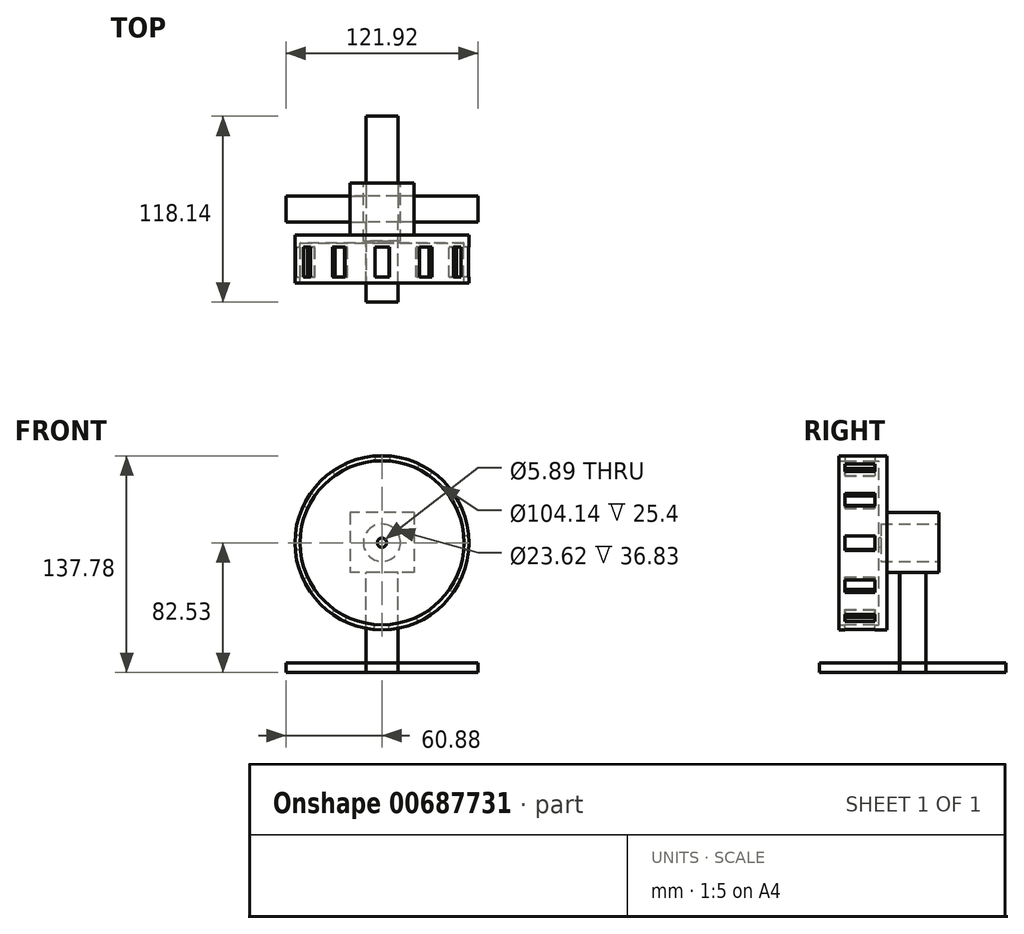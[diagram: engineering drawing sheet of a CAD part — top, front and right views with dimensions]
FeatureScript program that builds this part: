
annotation { "Feature Type Name" : "Feature", "Feature Type Description" : "" }
export const myFeature = defineFeature(function(context is Context, id is Id, definition is map)
    precondition{}
    {
        {
            var Q0;
            Q0=qCreatedBy(makeId("Front.planeOp"),FACE);
            var sketch = newSketch(context, id + "F0", { "sketchPlane" : qUnion([Q0])});
            skCircle(sketch, "E0", {"center": v(0, 0) * mm, "radius": 52.07 * mm});
            skCircle(sketch, "E1", {"center": v(0, 0) * mm, "radius": 55.24 * mm});
            skSolve(sketch);
        }
        {
            var Q0;
            Q0=makeQuery(id+"F0.imprint","IMPRINT",FACE,{"disambiguationData":[TD([[makeQuery(id+"F0.imprint","IMPRINT",EDGE,{"derivedFrom":sQuery(id+"F0.wireOp",EDGE,"E0")}),1.0]])]});
            extrude(context, id + "F1", {"entities" : qUnion([Q0]), "depth" : 5.08 * mm, "offsetDistance" : 25.4 * mm});
        }
        {
            var Q0;
            Q0=makeQuery(id+"F0.imprint","IMPRINT",FACE,{"disambiguationData":[TD([[makeQuery(id+"F0.imprint","IMPRINT",EDGE,{"derivedFrom":sQuery(id+"F0.wireOp",EDGE,"E0")}),-1.0]])]});
            extrude(context, id + "F2", {"entities" : qUnion([Q0]), "operationType" : NewBodyOperationType.ADD, "depth" : 30.48 * mm, "offsetDistance" : 25.4 * mm});
        }
        {
            var Q0;
            Q0=makeQuery(id+"F1.opExtrude","CAP_FACE",FACE,{"disambiguationData":[OSD([sQuery(id+"F0.wireOp",EDGE,"E0")])],"isStart":false});
            var sketch = newSketch(context, id + "F3", { "sketchPlane" : qUnion([Q0])});
            skCircle(sketch, "E2.cCircle", {"center": v(0, 0) * mm, "radius": 17.26 * mm, "construction": true});
            skLineSegment(sketch, "E2.0", {"start": v(12.58, -12.7) * mm, "end": v(4.55, -17.28) * mm});
            skLineSegment(sketch, "E2.1", {"start": v(4.55, -17.28) * mm, "end": v(-4.7, -17.24) * mm});
            skLineSegment(sketch, "E2.2", {"start": v(-4.7, -17.24) * mm, "end": v(-12.7, -12.58) * mm});
            skLineSegment(sketch, "E2.3", {"start": v(-12.7, -12.58) * mm, "end": v(-17.28, -4.55) * mm});
            skLineSegment(sketch, "E2.4", {"start": v(-17.28, -4.55) * mm, "end": v(-17.24, 4.7) * mm});
            skLineSegment(sketch, "E2.5", {"start": v(-17.24, 4.7) * mm, "end": v(-12.58, 12.7) * mm});
            skLineSegment(sketch, "E2.6", {"start": v(-12.58, 12.7) * mm, "end": v(-4.55, 17.28) * mm});
            skLineSegment(sketch, "E2.7", {"start": v(-4.55, 17.28) * mm, "end": v(4.7, 17.24) * mm});
            skLineSegment(sketch, "E2.8", {"start": v(4.7, 17.24) * mm, "end": v(12.7, 12.58) * mm});
            skLineSegment(sketch, "E2.9", {"start": v(12.7, 12.58) * mm, "end": v(17.28, 4.55) * mm});
            skLineSegment(sketch, "E2.10", {"start": v(17.28, 4.55) * mm, "end": v(17.24, -4.7) * mm});
            skLineSegment(sketch, "E2.11", {"start": v(17.24, -4.7) * mm, "end": v(12.58, -12.7) * mm});
            skPoint(sketch, "E2.0.midPoint", {"position": v(8.57, -14.99) * mm});
            skSolve(sketch);
        }
        {
            var Q0;
            Q0=makeQuery(id+"F3.imprint","IMPRINT",FACE,{"disambiguationData":[TD([[makeQuery(id+"F3.imprint","IMPRINT",EDGE,{"derivedFrom":sQuery(id+"F3.wireOp",EDGE,"E2.0")}),-1.0]])]});
            extrude(context, id + "F4", {"entities" : qUnion([Q0]), "operationType" : NewBodyOperationType.ADD, "depth" : 21.59 * mm, "offsetDistance" : 25.4 * mm});
        }
        {
            var Q0;
            Q0=makeQuery(id+"F4.opExtrude","SWEPT_FACE",FACE,{"disambiguationData":[OSD([sQuery(id+"F3.wireOp",EDGE,"E2.8")])]});
            var sketch = newSketch(context, id + "F5", { "sketchPlane" : qUnion([Q0])});
            skLineSegment(sketch, "E3", {"start": v(-4.63, -7.62) * mm, "end": v(4.63, -7.62) * mm});
            skSolve(sketch);
        }
        {
            var Q0;
            {var subQ0=sQuery(id+"F5.wireOp",EDGE,"E3");Q0=makeQuery(id+"F5.imprint","IMPRINT",FACE,{"disambiguationData":[TD([[makeQuery(id+"F5.imprint","IMPRINT",EDGE,{"derivedFrom":subQ0}),-1.0]])]});}
            extrude(context, id + "F6", {"entities" : qUnion([Q0]), "operationType" : NewBodyOperationType.REMOVE, "depth" : 50.8 * mm, "offsetDistance" : 25.4 * mm});
        }
        {
            var Q0;
            Q0=makeQuery(id+"F4.opExtrude","SWEPT_FACE",FACE,{"disambiguationData":[OSD([sQuery(id+"F3.wireOp",EDGE,"E2.7")])]});
            var sketch = newSketch(context, id + "F7", { "sketchPlane" : qUnion([Q0])});
            skLineSegment(sketch, "E4", {"start": v(4.63, -7.62) * mm, "end": v(-4.63, -7.62) * mm});
            skSolve(sketch);
        }
        {
            var Q0;
            {var subQ0=sQuery(id+"F7.wireOp",EDGE,"E4");Q0=makeQuery(id+"F7.imprint","IMPRINT",FACE,{"disambiguationData":[TD([[makeQuery(id+"F7.imprint","IMPRINT",EDGE,{"derivedFrom":subQ0}),1.0]])]});}
            extrude(context, id + "F8", {"entities" : qUnion([Q0]), "operationType" : NewBodyOperationType.REMOVE, "depth" : 50.8 * mm, "offsetDistance" : 25.4 * mm});
        }
        {
            var Q0;
            Q0=makeQuery(id+"F4.opExtrude","SWEPT_FACE",FACE,{"disambiguationData":[OSD([sQuery(id+"F3.wireOp",EDGE,"E2.6")])]});
            var sketch = newSketch(context, id + "F9", { "sketchPlane" : qUnion([Q0])});
            skLineSegment(sketch, "E5", {"start": v(4.63, -7.62) * mm, "end": v(-4.63, -7.62) * mm});
            skSolve(sketch);
        }
        {
            var Q0;
            {var subQ0=sQuery(id+"F9.wireOp",EDGE,"E5");Q0=makeQuery(id+"F9.imprint","IMPRINT",FACE,{"disambiguationData":[TD([[makeQuery(id+"F9.imprint","IMPRINT",EDGE,{"derivedFrom":subQ0}),1.0]])]});}
            extrude(context, id + "F10", {"entities" : qUnion([Q0]), "operationType" : NewBodyOperationType.REMOVE, "depth" : 50.8 * mm, "offsetDistance" : 25.4 * mm});
        }
        {
            var Q0;
            Q0=makeQuery(id+"F4.opExtrude","SWEPT_FACE",FACE,{"disambiguationData":[OSD([sQuery(id+"F3.wireOp",EDGE,"E2.5")])]});
            var sketch = newSketch(context, id + "F11", { "sketchPlane" : qUnion([Q0])});
            skLineSegment(sketch, "E6", {"start": v(7.62, 4.63) * mm, "end": v(7.62, -4.63) * mm});
            skSolve(sketch);
        }
        {
            var Q0;
            {var subQ0=sQuery(id+"F11.wireOp",EDGE,"E6");Q0=makeQuery(id+"F11.imprint","IMPRINT",FACE,{"disambiguationData":[TD([[makeQuery(id+"F11.imprint","IMPRINT",EDGE,{"derivedFrom":subQ0}),1.0]])]});}
            extrude(context, id + "F12", {"entities" : qUnion([Q0]), "operationType" : NewBodyOperationType.REMOVE, "depth" : 50.8 * mm, "offsetDistance" : 25.4 * mm});
        }
        {
            var Q0;
            Q0=makeQuery(id+"F4.opExtrude","SWEPT_FACE",FACE,{"disambiguationData":[OSD([sQuery(id+"F3.wireOp",EDGE,"E2.4")])]});
            var sketch = newSketch(context, id + "F13", { "sketchPlane" : qUnion([Q0])});
            skLineSegment(sketch, "E7", {"start": v(7.62, 4.63) * mm, "end": v(7.62, -4.63) * mm});
            skSolve(sketch);
        }
        {
            var Q0;
            {var subQ0=sQuery(id+"F13.wireOp",EDGE,"E7");Q0=makeQuery(id+"F13.imprint","IMPRINT",FACE,{"disambiguationData":[TD([[makeQuery(id+"F13.imprint","IMPRINT",EDGE,{"derivedFrom":subQ0}),1.0]])]});}
            extrude(context, id + "F14", {"entities" : qUnion([Q0]), "operationType" : NewBodyOperationType.REMOVE, "depth" : 50.8 * mm, "offsetDistance" : 25.4 * mm});
        }
        {
            var Q0;
            Q0=makeQuery(id+"F4.opExtrude","SWEPT_FACE",FACE,{"disambiguationData":[OSD([sQuery(id+"F3.wireOp",EDGE,"E2.3")])]});
            var sketch = newSketch(context, id + "F15", { "sketchPlane" : qUnion([Q0])});
            skLineSegment(sketch, "E8", {"start": v(7.62, 4.63) * mm, "end": v(7.62, -4.63) * mm});
            skSolve(sketch);
        }
        {
            var Q0;
            {var subQ0=sQuery(id+"F15.wireOp",EDGE,"E8");Q0=makeQuery(id+"F15.imprint","IMPRINT",FACE,{"disambiguationData":[TD([[makeQuery(id+"F15.imprint","IMPRINT",EDGE,{"derivedFrom":subQ0}),1.0]])]});}
            extrude(context, id + "F16", {"entities" : qUnion([Q0]), "operationType" : NewBodyOperationType.REMOVE, "depth" : 50.8 * mm, "offsetDistance" : 25.4 * mm});
        }
        {
            var Q0;
            Q0=makeQuery(id+"F4.opExtrude","SWEPT_FACE",FACE,{"disambiguationData":[OSD([sQuery(id+"F3.wireOp",EDGE,"E2.2")])]});
            var sketch = newSketch(context, id + "F17", { "sketchPlane" : qUnion([Q0])});
            skLineSegment(sketch, "E9", {"start": v(-4.63, 7.62) * mm, "end": v(4.63, 7.62) * mm});
            skSolve(sketch);
        }
        {
            var Q0;
            {var subQ0=sQuery(id+"F17.wireOp",EDGE,"E9");Q0=makeQuery(id+"F17.imprint","IMPRINT",FACE,{"disambiguationData":[TD([[makeQuery(id+"F17.imprint","IMPRINT",EDGE,{"derivedFrom":subQ0}),1.0]])]});}
            extrude(context, id + "F18", {"entities" : qUnion([Q0]), "operationType" : NewBodyOperationType.REMOVE, "depth" : 50.8 * mm, "offsetDistance" : 25.4 * mm});
        }
        {
            var Q0;
            Q0=makeQuery(id+"F4.opExtrude","SWEPT_FACE",FACE,{"disambiguationData":[OSD([sQuery(id+"F3.wireOp",EDGE,"E2.1")])]});
            var sketch = newSketch(context, id + "F19", { "sketchPlane" : qUnion([Q0])});
            skLineSegment(sketch, "E10", {"start": v(-4.63, 7.62) * mm, "end": v(4.63, 7.62) * mm});
            skSolve(sketch);
        }
        {
            var Q0;
            {var subQ0=sQuery(id+"F19.wireOp",EDGE,"E10");Q0=makeQuery(id+"F19.imprint","IMPRINT",FACE,{"disambiguationData":[TD([[makeQuery(id+"F19.imprint","IMPRINT",EDGE,{"derivedFrom":subQ0}),1.0]])]});}
            extrude(context, id + "F20", {"entities" : qUnion([Q0]), "operationType" : NewBodyOperationType.REMOVE, "depth" : 50.8 * mm, "offsetDistance" : 25.4 * mm});
        }
        {
            var Q0;
            Q0=makeQuery(id+"F4.opExtrude","SWEPT_FACE",FACE,{"disambiguationData":[OSD([sQuery(id+"F3.wireOp",EDGE,"E2.0")])]});
            var sketch = newSketch(context, id + "F21", { "sketchPlane" : qUnion([Q0])});
            skLineSegment(sketch, "E11", {"start": v(-4.63, 7.62) * mm, "end": v(4.63, 7.62) * mm});
            skSolve(sketch);
        }
        {
            var Q0;
            {var subQ0=sQuery(id+"F21.wireOp",EDGE,"E11");Q0=makeQuery(id+"F21.imprint","IMPRINT",FACE,{"disambiguationData":[TD([[makeQuery(id+"F21.imprint","IMPRINT",EDGE,{"derivedFrom":subQ0}),1.0]])]});}
            extrude(context, id + "F22", {"entities" : qUnion([Q0]), "operationType" : NewBodyOperationType.REMOVE, "depth" : 50.8 * mm, "offsetDistance" : 25.4 * mm});
        }
        {
            var Q0;
            Q0=makeQuery(id+"F4.opExtrude","SWEPT_FACE",FACE,{"disambiguationData":[OSD([sQuery(id+"F3.wireOp",EDGE,"E2.11")])]});
            var sketch = newSketch(context, id + "F23", { "sketchPlane" : qUnion([Q0])});
            skLineSegment(sketch, "E12", {"start": v(-7.62, -4.63) * mm, "end": v(-7.62, 4.63) * mm});
            skSolve(sketch);
        }
        {
            var Q0;
            {var subQ0=sQuery(id+"F23.wireOp",EDGE,"E12");Q0=makeQuery(id+"F23.imprint","IMPRINT",FACE,{"disambiguationData":[TD([[makeQuery(id+"F23.imprint","IMPRINT",EDGE,{"derivedFrom":subQ0}),1.0]])]});}
            extrude(context, id + "F24", {"entities" : qUnion([Q0]), "operationType" : NewBodyOperationType.REMOVE, "depth" : 50.8 * mm, "offsetDistance" : 25.4 * mm});
        }
        {
            var Q0;
            Q0=makeQuery(id+"F4.opExtrude","SWEPT_FACE",FACE,{"disambiguationData":[OSD([sQuery(id+"F3.wireOp",EDGE,"E2.10")])]});
            var sketch = newSketch(context, id + "F25", { "sketchPlane" : qUnion([Q0])});
            skLineSegment(sketch, "E13", {"start": v(-7.62, 4.63) * mm, "end": v(-7.62, -4.63) * mm});
            skSolve(sketch);
        }
        {
            var Q0;
            {var subQ0=sQuery(id+"F25.wireOp",EDGE,"E13");Q0=makeQuery(id+"F25.imprint","IMPRINT",FACE,{"disambiguationData":[TD([[makeQuery(id+"F25.imprint","IMPRINT",EDGE,{"derivedFrom":subQ0}),-1.0]])]});}
            extrude(context, id + "F26", {"entities" : qUnion([Q0]), "operationType" : NewBodyOperationType.REMOVE, "depth" : 50.8 * mm, "offsetDistance" : 25.4 * mm});
        }
        {
            var Q0;
            Q0=makeQuery(id+"F4.opExtrude","SWEPT_FACE",FACE,{"disambiguationData":[OSD([sQuery(id+"F3.wireOp",EDGE,"E2.9")])]});
            var sketch = newSketch(context, id + "F27", { "sketchPlane" : qUnion([Q0])});
            skLineSegment(sketch, "E14", {"start": v(-7.62, 4.63) * mm, "end": v(-7.62, -4.63) * mm});
            skSolve(sketch);
        }
        {
            var Q0;
            {var subQ0=sQuery(id+"F27.wireOp",EDGE,"E14");Q0=makeQuery(id+"F27.imprint","IMPRINT",FACE,{"disambiguationData":[TD([[makeQuery(id+"F27.imprint","IMPRINT",EDGE,{"derivedFrom":subQ0}),-1.0]])]});}
            extrude(context, id + "F28", {"entities" : qUnion([Q0]), "operationType" : NewBodyOperationType.REMOVE, "depth" : 50.8 * mm, "offsetDistance" : 25.4 * mm});
        }
        {
            var Q0;
            Q0=makeQuery(id+"F0.imprint","IMPRINT",FACE,{"disambiguationData":[TD([[makeQuery(id+"F0.imprint","IMPRINT",EDGE,{"derivedFrom":sQuery(id+"F0.wireOp",EDGE,"E0")}),1.0]])]});
            var sketch = newSketch(context, id + "F29", { "sketchPlane" : qUnion([Q0])});
            skLineSegment(sketch, "E15.bottom", {"start": v(20.4, 19.07) * mm, "end": v(-20.24, 19.07) * mm});
            skLineSegment(sketch, "E15.top", {"start": v(20.4, -19.03) * mm, "end": v(-20.24, -19.03) * mm});
            skLineSegment(sketch, "E15.left", {"start": v(20.4, 19.07) * mm, "end": v(20.4, -19.03) * mm});
            skLineSegment(sketch, "E15.right", {"start": v(-20.24, 19.07) * mm, "end": v(-20.24, -19.03) * mm});
            skSolve(sketch);
        }
        {
            var Q0;
            Q0=makeQuery(id+"F29.imprint","IMPRINT",FACE,{"disambiguationData":[TD([[makeQuery(id+"F29.imprint","IMPRINT",EDGE,{"derivedFrom":sQuery(id+"F29.wireOp",EDGE,"E15.bottom")}),1.0]])]});
            extrude(context, id + "F30", {"entities" : qUnion([Q0]), "operationType" : NewBodyOperationType.ADD, "oppositeDirection" : true, "depth" : 33.02 * mm, "offsetDistance" : 25.4 * mm});
        }
        {
            var Q0;
            Q0=makeQuery(id+"F4.opExtrude","CAP_FACE",FACE,{"disambiguationData":[OSD([sQuery(id+"F3.wireOp",EDGE,"E2.0"),sQuery(id+"F3.wireOp",EDGE,"E2.1"),sQuery(id+"F3.wireOp",EDGE,"E2.2"),sQuery(id+"F3.wireOp",EDGE,"E2.3"),sQuery(id+"F3.wireOp",EDGE,"E2.4"),sQuery(id+"F3.wireOp",EDGE,"E2.5"),sQuery(id+"F3.wireOp",EDGE,"E2.6"),sQuery(id+"F3.wireOp",EDGE,"E2.7"),sQuery(id+"F3.wireOp",EDGE,"E2.8"),sQuery(id+"F3.wireOp",EDGE,"E2.9"),sQuery(id+"F3.wireOp",EDGE,"E2.10"),sQuery(id+"F3.wireOp",EDGE,"E2.11")])],"isStart":false});
            extrude(context, id + "F31", {"entities" : qUnion([Q0]), "operationType" : NewBodyOperationType.REMOVE, "oppositeDirection" : true, "depth" : 21.59 * mm, "offsetDistance" : 25.4 * mm});
        }
        {
            var Q0;
            Q0=makeQuery(id+"F30.opExtrude","SWEPT_FACE",FACE,{"disambiguationData":[OSD([sQuery(id+"F29.wireOp",EDGE,"E15.top")])]});
            var sketch = newSketch(context, id + "F32", { "sketchPlane" : qUnion([Q0])});
            skLineSegment(sketch, "E16", {"start": v(0.08, -33.02) * mm, "end": v(-20.24, -16.51) * mm});
            skLineSegment(sketch, "E17", {"start": v(-20.24, -16.51) * mm, "end": v(0, 0) * mm});
            skLineSegment(sketch, "E18", {"start": v(0, 0) * mm, "end": v(20.4, -16.51) * mm});
            skLineSegment(sketch, "E19", {"start": v(20.4, -16.5) * mm, "end": v(0.08, -33.02) * mm});
            skPoint(sketch, "E20.oppositeSnap0", {"position": v(-10.08, -24.77) * mm});
            skLineSegment(sketch, "E20.bottom", {"start": v(10.24, -24.77) * mm, "end": v(-10.08, -24.77) * mm});
            skLineSegment(sketch, "E20.top", {"start": v(10.24, -8.22) * mm, "end": v(-10.08, -8.22) * mm});
            skLineSegment(sketch, "E20.left", {"start": v(10.24, -24.77) * mm, "end": v(10.24, -8.22) * mm});
            skLineSegment(sketch, "E20.right", {"start": v(-10.08, -24.77) * mm, "end": v(-10.08, -8.22) * mm});
            skSolve(sketch);
        }
        {
            var Q0;
            {var subQ1=sQuery(id+"F32.wireOp",EDGE,"E20.bottom");Q0=makeQuery(id+"F32.imprint","IMPRINT",FACE,{"disambiguationData":[TD([[makeQuery(id+"F32.imprint","IMPRINT",EDGE,{"derivedFrom":subQ1}),-1.0]])]});}
            extrude(context, id + "F33", {"entities" : qUnion([Q0]), "operationType" : NewBodyOperationType.ADD, "depth" : 63.5 * mm, "offsetDistance" : 25.4 * mm});
        }
        {
            var Q0;
            Q0=makeQuery(id+"F33.opExtrude","SWEPT_FACE",FACE,{"disambiguationData":[OSD([sQuery(id+"F32.wireOp",EDGE,"E20.top")])]});
            var sketch = newSketch(context, id + "F34", { "sketchPlane" : qUnion([Q0])});
            skLineSegment(sketch, "E21", {"start": v(-10.08, -76.22) * mm, "end": v(10.16, -76.22) * mm});
            skSolve(sketch);
        }
        {
            var Q0;
            {var subQ0=sQuery(id+"F34.wireOp",EDGE,"E21");Q0=makeQuery(id+"F34.imprint","IMPRINT",FACE,{"disambiguationData":[TD([[makeQuery(id+"F34.imprint","IMPRINT",EDGE,{"derivedFrom":subQ0}),-1.0]])]});}
            extrude(context, id + "F35", {"entities" : qUnion([Q0]), "operationType" : NewBodyOperationType.ADD, "depth" : 50.8 * mm, "offsetDistance" : 25.4 * mm});
        }
        {
            var Q0;
            {var subQ0=sQuery(id+"F32.wireOp",EDGE,"E20.right");Q0=makeQuery(id+"F35.boolean.opBoolean","MERGE",FACE,{"derivedFrom":[makeQuery(id+"F33.opExtrude","SWEPT_FACE",FACE,{"disambiguationData":[OSD([subQ0])]}),makeQuery(id+"F35.opExtrude","SWEPT_FACE",FACE,{"disambiguationData":[OSD([sQuery(id+"F32.wireOp",EDGE,"E17"),sQuery(id+"F32.wireOp",EDGE,"E20.top"),subQ0])]})]});}
            var sketch = newSketch(context, id + "F36", { "sketchPlane" : qUnion([Q0])});
            skLineSegment(sketch, "E22", {"start": v(-8.22, -76.22) * mm, "end": v(-24.77, -76.22) * mm});
            skLineSegment(sketch, "E23", {"start": v(-8.22, -76.22) * mm, "end": v(-8.22, -82.53) * mm});
            skSolve(sketch);
        }
        {
            var Q0;
            {var subQ0=sQuery(id+"F36.wireOp",EDGE,"E22");Q0=makeQuery(id+"F36.imprint","IMPRINT",FACE,{"disambiguationData":[TD([[makeQuery(id+"F36.imprint","IMPRINT",EDGE,{"derivedFrom":subQ0}),1.0]])]});}
            extrude(context, id + "F37", {"entities" : qUnion([Q0]), "operationType" : NewBodyOperationType.ADD, "depth" : 50.8 * mm, "offsetDistance" : 25.4 * mm});
        }
        {
            var Q0;
            {var subQ0=sQuery(id+"F32.wireOp",EDGE,"E20.bottom");Q0=makeQuery(id+"F37.boolean.opBoolean","MERGE",FACE,{"derivedFrom":[makeQuery(id+"F33.opExtrude","SWEPT_FACE",FACE,{"disambiguationData":[OSD([subQ0])]}),makeQuery(id+"F37.opExtrude","SWEPT_FACE",FACE,{"disambiguationData":[OSD([sQuery(id+"F32.wireOp",EDGE,"E16"),subQ0,sQuery(id+"F32.wireOp",EDGE,"E20.right")])]})]});}
            var sketch = newSketch(context, id + "F38", { "sketchPlane" : qUnion([Q0])});
            skLineSegment(sketch, "E24", {"start": v(10.08, -76.22) * mm, "end": v(10.08, -82.53) * mm});
            skLineSegment(sketch, "E25", {"start": v(10.08, -76.22) * mm, "end": v(-10.24, -76.22) * mm});
            skSolve(sketch);
        }
        {
            var Q0;
            {var subQ0=sQuery(id+"F38.wireOp",EDGE,"E24");Q0=makeQuery(id+"F38.imprint","IMPRINT",FACE,{"disambiguationData":[TD([[makeQuery(id+"F38.imprint","IMPRINT",EDGE,{"derivedFrom":subQ0}),-1.0]])]});}
            extrude(context, id + "F39", {"entities" : qUnion([Q0]), "operationType" : NewBodyOperationType.ADD, "depth" : 50.8 * mm, "offsetDistance" : 25.4 * mm});
        }
        {
            var Q0;
            {var subQ0=sQuery(id+"F32.wireOp",EDGE,"E20.left");Q0=makeQuery(id+"F39.boolean.opBoolean","MERGE",FACE,{"derivedFrom":[makeQuery(id+"F33.opExtrude","SWEPT_FACE",FACE,{"disambiguationData":[OSD([subQ0])]}),makeQuery(id+"F39.opExtrude","SWEPT_FACE",FACE,{"disambiguationData":[OSD([sQuery(id+"F32.wireOp",EDGE,"E19"),sQuery(id+"F32.wireOp",EDGE,"E20.bottom"),subQ0])]})]});}
            var sketch = newSketch(context, id + "F40", { "sketchPlane" : qUnion([Q0])});
            skLineSegment(sketch, "E26", {"start": v(24.76, -76.22) * mm, "end": v(8.29, -76.22) * mm});
            skLineSegment(sketch, "E27", {"start": v(24.76, -76.22) * mm, "end": v(24.76, -82.53) * mm});
            skSolve(sketch);
        }
        {
            var Q0;
            {var subQ0=sQuery(id+"F40.wireOp",EDGE,"E26");Q0=makeQuery(id+"F40.imprint","IMPRINT",FACE,{"disambiguationData":[TD([[makeQuery(id+"F40.imprint","IMPRINT",EDGE,{"derivedFrom":subQ0}),1.0]])]});}
            extrude(context, id + "F41", {"entities" : qUnion([Q0]), "operationType" : NewBodyOperationType.ADD, "depth" : 50.8 * mm, "offsetDistance" : 25.4 * mm});
        }
        {
            var Q0;
            Q0=makeQuery(id+"F30.opExtrude","CAP_FACE",FACE,{"disambiguationData":[OSD([sQuery(id+"F29.wireOp",EDGE,"E15.bottom"),sQuery(id+"F29.wireOp",EDGE,"E15.top"),sQuery(id+"F29.wireOp",EDGE,"E15.left"),sQuery(id+"F29.wireOp",EDGE,"E15.right")])],"isStart":false});
            var sketch = newSketch(context, id + "F42", { "sketchPlane" : qUnion([Q0])});
            skCircle(sketch, "E28", {"center": v(0, 0) * mm, "radius": 11.81 * mm});
            skSolve(sketch);
        }
        {
            var Q0;
            Q0=makeQuery(id+"F31.boolean.opBoolean","MERGE",FACE,{"derivedFrom":[makeQuery(id+"F1.opExtrude","CAP_FACE",FACE,{"disambiguationData":[OSD([sQuery(id+"F0.wireOp",EDGE,"E0")])],"isStart":false}),makeQuery(id+"F31.opExtrude","CAP_FACE",FACE,{"disambiguationData":[OSD([sQuery(id+"F3.wireOp",EDGE,"E2.0"),sQuery(id+"F3.wireOp",EDGE,"E2.1"),sQuery(id+"F3.wireOp",EDGE,"E2.2"),sQuery(id+"F3.wireOp",EDGE,"E2.3"),sQuery(id+"F3.wireOp",EDGE,"E2.4"),sQuery(id+"F3.wireOp",EDGE,"E2.5"),sQuery(id+"F3.wireOp",EDGE,"E2.6"),sQuery(id+"F3.wireOp",EDGE,"E2.7"),sQuery(id+"F3.wireOp",EDGE,"E2.8"),sQuery(id+"F3.wireOp",EDGE,"E2.9"),sQuery(id+"F3.wireOp",EDGE,"E2.10"),sQuery(id+"F3.wireOp",EDGE,"E2.11")])],"isStart":false})]});
            var sketch = newSketch(context, id + "F43", { "sketchPlane" : qUnion([Q0])});
            skCircle(sketch, "E29", {"center": v(0, 0) * mm, "radius": 2.95 * mm});
            skSolve(sketch);
        }
        {
            var Q0;
            Q0=makeQuery(id+"F43.imprint","IMPRINT",FACE,{"disambiguationData":[TD([[makeQuery(id+"F43.imprint","IMPRINT",EDGE,{"derivedFrom":sQuery(id+"F43.wireOp",EDGE,"E29")}),1.0]])]});
            extrude(context, id + "F44", {"entities" : qUnion([Q0]), "operationType" : NewBodyOperationType.REMOVE, "oppositeDirection" : true, "depth" : 1.63 * mm, "offsetDistance" : 25.4 * mm});
        }
        {
            var Q0;
            Q0=makeQuery(id+"F42.imprint","IMPRINT",FACE,{"disambiguationData":[TD([[makeQuery(id+"F42.imprint","IMPRINT",EDGE,{"derivedFrom":sQuery(id+"F42.wireOp",EDGE,"E28")}),1.0]])]});
            extrude(context, id + "F45", {"entities" : qUnion([Q0]), "operationType" : NewBodyOperationType.REMOVE, "oppositeDirection" : true, "depth" : 36.83 * mm, "offsetDistance" : 25.4 * mm});
        }
    });
